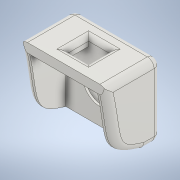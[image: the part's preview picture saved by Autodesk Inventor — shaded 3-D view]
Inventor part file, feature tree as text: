
AUTODESK INVENTOR PART (.ipt)
format: ipt  version: 2021 (Build 250183000, 183)  size: 264,704 bytes
history: native  units: mm
features: extrude x8, sketch x8, projected_geometry x4, fillet x2
ambient origin geometry x8: Origin, YZ Plane, XZ Plane, XY Plane, X Axis, Y Axis, Z Axis, Center Point
bodies: Solid1 (feature_tree)
feature tree (22):
  extrude  "Extrusion1"  Depth=30.0mm
  extrude  "Extrusion2"  Depth=15.0mm
  extrude  "Extrusion3"  Depth=2.0mm
  extrude  "Extrusion4"  Depth=10.0mm
  extrude  "Extrusion5"  Depth=10.0mm
  extrude  "Extrusion6"  Depth=2.0mm TaperAngle=0.0deg
  extrude  "Extrusion7"  Depth=4.0mm TaperAngle=0.0deg
  extrude  "Extrusion8"  Depth=2.0mm
  fillet  "Fillet1"  Radius=3.0mm
  fillet  "Fillet2"  [1 undecoded]
  sketch  "Sketch1"  dims[d0=22.2mm d1=30.0mm]
  sketch  "Sketch2"  dims[d2=7.0mm d3=0.0mm d4=15.0mm]
  projected_geometry  "Projected Loop1"
  sketch  "Sketch3"  dims[d5=1.0mm d6=0.0mm d7=2.0mm]
  sketch  "Sketch4"  dims[d8=10.0mm d9=0.0mm d10=10.0mm]
  sketch  "Sketch5"  dims[d11=10.0mm d12=10.0mm]
  projected_geometry  "Projected Loop2"
  sketch  "Sketch6"  dims[d13=10.0mm d14=0.0mm d15=2.0mm d16=0.0mm]
  sketch  "Sketch7"  dims[d17=6.0mm d18=0.0mm d19=4.0mm d20=0.0mm]
  projected_geometry  "Projected Loop3"
  sketch  "Sketch8"  dims[d21=4.0mm d22=0.0mm d23=2.0mm d24=3.0mm]
  projected_geometry  "Projected Loop4"
note: 1 required parameter value undecoded (feature->parameter linkage not recoverable at this tier; creation-order binding heuristic only, values carry confidence <= 0.55)
